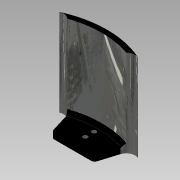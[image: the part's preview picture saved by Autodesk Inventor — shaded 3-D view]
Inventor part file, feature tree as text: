
AUTODESK INVENTOR PART (.ipt)
format: ipt  version: 2015 SP1 (Build 190203100, 203)  size: 167,424 bytes
history: native  units: mm
features: extrude x3, sketch x3, chamfer x1
ambient origin geometry x8: Origin, YZ Plane, XZ Plane, XY Plane, X Axis, Y Axis, Z Axis, Center Point
bodies: Solid1 (feature_tree)
feature tree (7):
  extrude  "Extrusion1"  Depth=5.0mm
  extrude  "Extrusion2"  Depth=1.291142mm
  extrude  "Extrusion3"  Depth=5.0mm
  chamfer  "Chamfer1"  Distance=20.705869mm
  sketch  "Sketch1"  dims[d0=5.0mm d1=2.0mm d2=2.5mm d3=2.5mm d4=34.377204mm]
  sketch  "Sketch2"  dims[d5=1.286842mm d6=1.291142mm]
  sketch  "Sketch3"  dims[d7=5.0mm d8=7.0mm d9=20.705869mm d10=10.020291mm d11=10.020291mm d12=13.361299mm d13=14.82011mm d14=53.698015mm d15=7.320812mm d16=3.0mm d17=0.0mm d18=3.5mm d19=46.0mm d20=0.0mm d21=3.0mm d22=1.907681mm d23=2.0mm d24=0.0mm d25=1.9mm d26=2.0mm d27=45.0deg]
